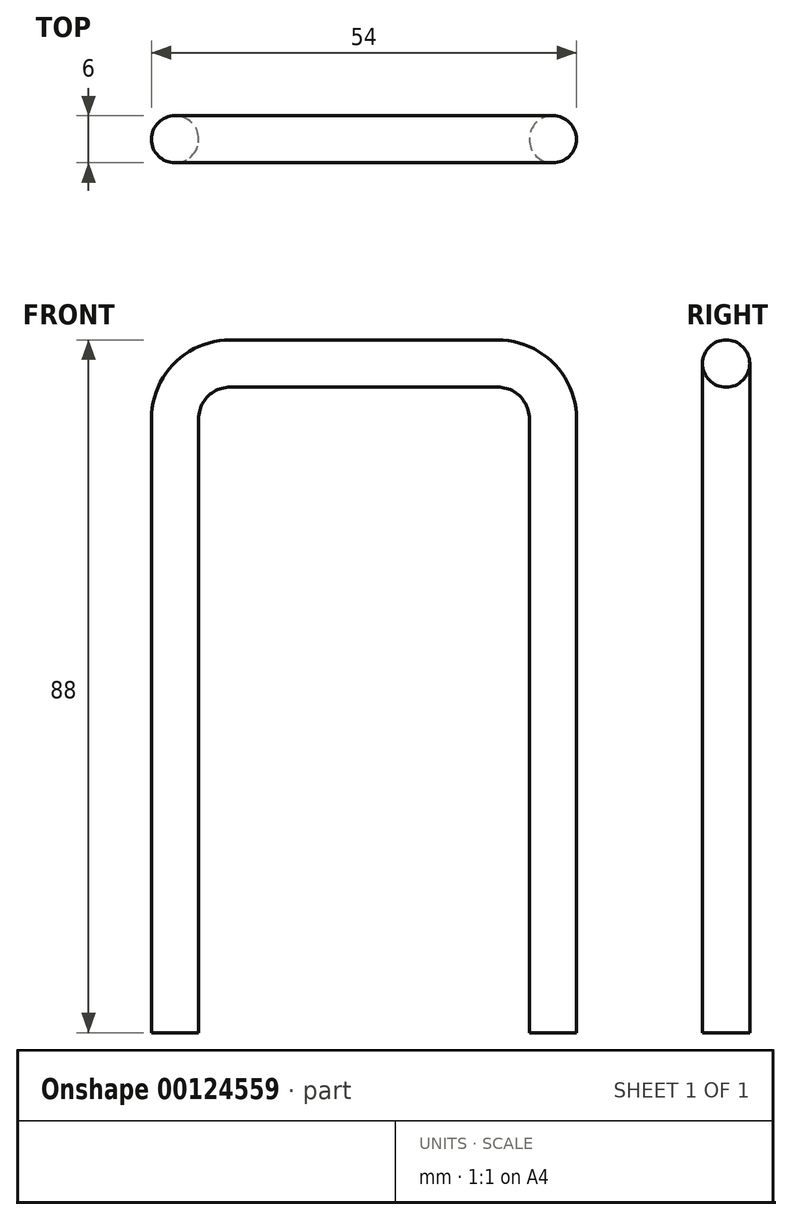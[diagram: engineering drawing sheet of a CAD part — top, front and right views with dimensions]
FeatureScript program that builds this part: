
annotation { "Feature Type Name" : "Feature", "Feature Type Description" : "" }
export const myFeature = defineFeature(function(context is Context, id is Id, definition is map)
    precondition{}
    {
        {
            var Q0;
            Q0=qCreatedBy(makeId("Front.planeOp"),FACE);
            var sketch = newSketch(context, id + "F0", { "sketchPlane" : qUnion([Q0])});
            skLineSegment(sketch, "E0.bottom", {"start": v(-17, 82) * mm, "end": v(17, 82) * mm});
            skLineSegment(sketch, "E0.left", {"start": v(-21, 78) * mm, "end": v(-21, 0) * mm});
            skLineSegment(sketch, "E0.right", {"start": v(21, 78) * mm, "end": v(21, 0) * mm});
            skPoint(sketch, "E1.visualSharp", {"position": v(-21, 82) * mm});
            skArc(sketch, "E1.filletArc", {"start": v(-17, 82) * mm, "mid": v(-19.83, 80.83) * mm, "end": v(-21, 78) * mm});
            skPoint(sketch, "E2.visualSharp", {"position": v(21, 82) * mm});
            skArc(sketch, "E2.filletArc", {"start": v(21, 78) * mm, "mid": v(19.83, 80.83) * mm, "end": v(17, 82) * mm});
            skSolve(sketch);
        }
        {
            var Q0;
            Q0=qCreatedBy(makeId("Top.planeOp"),FACE);
            var sketch = newSketch(context, id + "F1", { "sketchPlane" : qUnion([Q0])});
            skCircle(sketch, "E3", {"center": v(-24, 0) * mm, "radius": 3 * mm});
            skSolve(sketch);
        }
        {
            var Q0;
            Q0=makeQuery(id+"F1.imprint","IMPRINT",FACE,{"disambiguationData":[TD([[makeQuery(id+"F1.imprint","IMPRINT",EDGE,{"derivedFrom":sQuery(id+"F1.wireOp",EDGE,"E3")}),1.0]])]});
            var Q1;
            Q1 = qConstructionFilter(qBodyType(qCreatedBy(id + "F0" ,EDGE), BodyType.WIRE), ConstructionObject.NO);
            sweep(context, id + "F2", {"profiles" : qUnion([Q0]), "path" : qUnion([Q1])});
        }
    });
